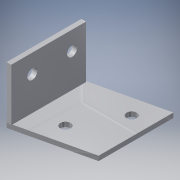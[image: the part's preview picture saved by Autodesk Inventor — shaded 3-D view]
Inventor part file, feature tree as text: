
AUTODESK INVENTOR PART (.ipt)
format: ipt  version: 2016 (Build 200138000, 138)  size: 150,016 bytes
history: native  units: in
note: dims shown in document units (in); Inventor stores cm internally (conversion verified against a paired STEP export)
features: extrude x5, sketch x4
ambient origin geometry x8: Origin, YZ Plane, XZ Plane, XY Plane, X Axis, Y Axis, Z Axis, Center Point
bodies: Solid1 (feature_tree)
feature tree (9):
  extrude  "Extrusion1"  Depth=2.0in
  extrude  "Extrusion2"  Depth=0.9in
  sketch  "Sketch3"  dims[d9=0.9in d12=0.125in d13=0.0in]
  extrude  "Extrusion3"  Depth=0.125in TaperAngle=0.0deg
  extrude  "Extrusion4"  Depth=0.125in
  extrude  "Extrusion5"  Depth=0.125in
  sketch  "Sketch1"  dims[d4=2.0in d5=0.0in d6=0.2656in]
  sketch  "Sketch2"  dims[d7=0.2656in d8=0.9in]
  sketch  "Sketch4"  dims[d14=2.0in d15=0.125in d16=0.5625in d17=1.625in d18=0.0893in d19=0.2656in d20=0.266in d21=0.5in d22=2.0in d23=1.0in d24=0.8619in d26=0.5in d28=0.125in d29=0.0in d30=0.125in d31=0.0in d32=0.475in d33=0.125in d34=0.0in d35=1.883in d36=0.4912in d37=0.7369in]
